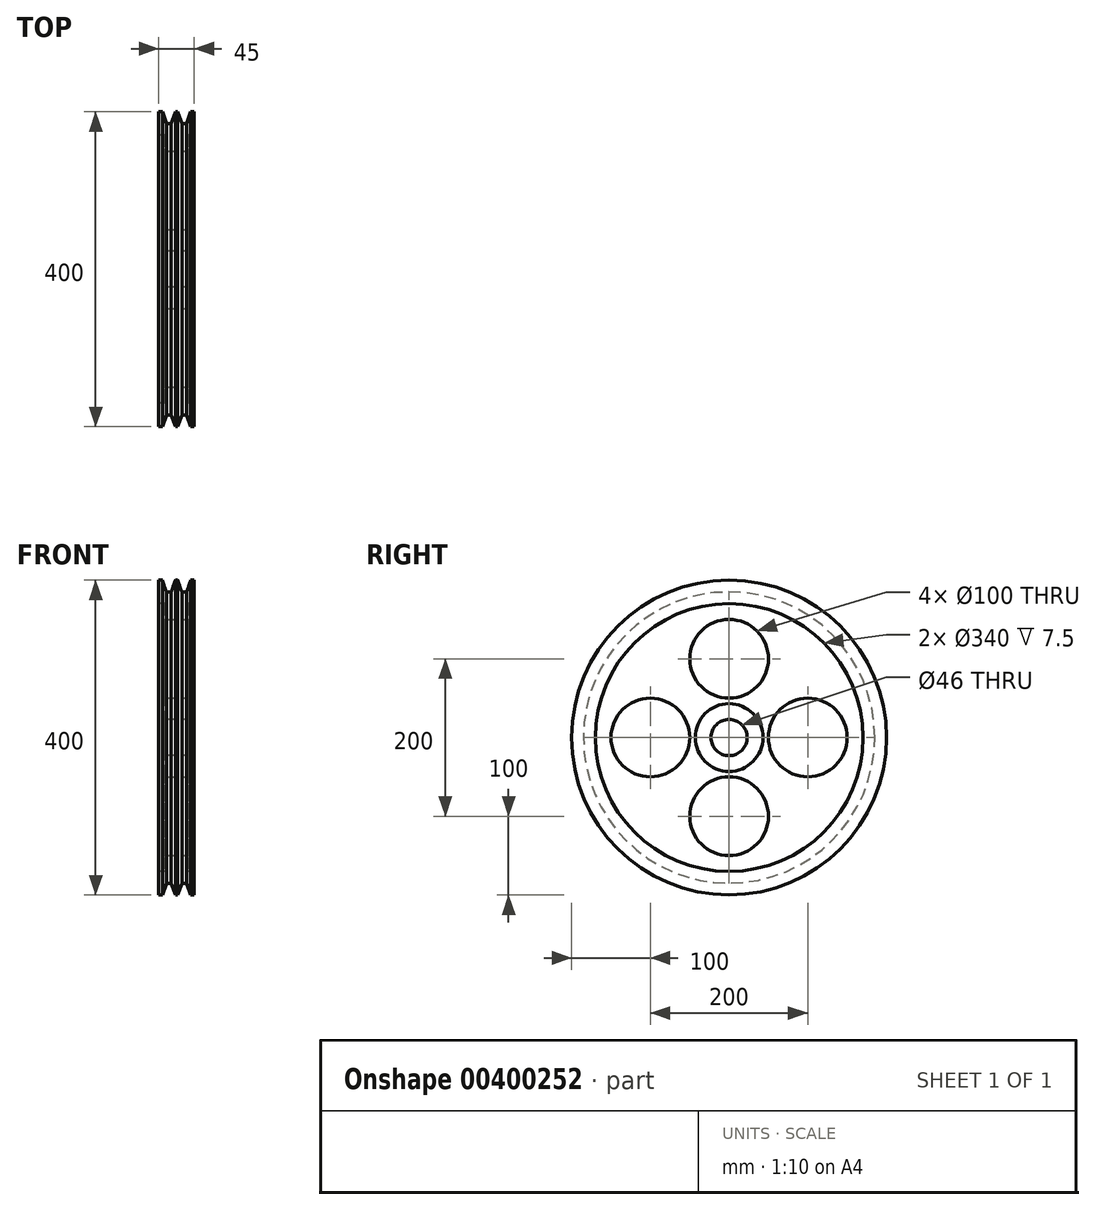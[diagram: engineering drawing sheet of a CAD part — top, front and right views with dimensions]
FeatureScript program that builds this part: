
annotation { "Feature Type Name" : "Feature", "Feature Type Description" : "" }
export const myFeature = defineFeature(function(context is Context, id is Id, definition is map)
    precondition{}
    {
        {
            var Q0;
            Q0=qCreatedBy(makeId("Front.planeOp"),FACE);
            var sketch = newSketch(context, id + "F0", { "sketchPlane" : qUnion([Q0])});
            skLineSegment(sketch, "E0", {"start": v(0, 0) * mm, "end": v(0, 346.48) * mm, "construction": true});
            skLineSegment(sketch, "E1", {"start": v(0, 170) * mm, "end": v(22.5, 170) * mm});
            skLineSegment(sketch, "E2", {"start": v(22.5, 200) * mm, "end": v(22.5, 170) * mm});
            skLineSegment(sketch, "E3", {"start": v(22.5, 200) * mm, "end": v(18, 200) * mm});
            skLineSegment(sketch, "E4", {"start": v(18, 200) * mm, "end": v(12.69, 185) * mm});
            skPoint(sketch, "E5.endSnap0", {"position": v(0, 170) * mm});
            skLineSegment(sketch, "E6", {"start": v(12.69, 185) * mm, "end": v(6.81, 185) * mm});
            skLineSegment(sketch, "E7", {"start": v(1.5, 200) * mm, "end": v(6.81, 185) * mm});
            skLineSegment(sketch, "E8", {"start": v(1.5, 200) * mm, "end": v(0, 200) * mm});
            skLineSegment(sketch, "E9.MirrorCS", {"start": v(-1.5, 200) * mm, "end": v(0, 200) * mm});
            skLineSegment(sketch, "E10.MirrorCS", {"start": v(-18, 200) * mm, "end": v(-12.69, 185) * mm});
            skLineSegment(sketch, "E11.MirrorCS", {"start": v(-12.69, 185) * mm, "end": v(-6.81, 185) * mm});
            skLineSegment(sketch, "E12.MirrorCS", {"start": v(0, 170) * mm, "end": v(-22.5, 170) * mm});
            skLineSegment(sketch, "E13.MirrorCS", {"start": v(-22.5, 200) * mm, "end": v(-18, 200) * mm});
            skLineSegment(sketch, "E14.MirrorCS", {"start": v(-22.5, 200) * mm, "end": v(-22.5, 170) * mm});
            skLineSegment(sketch, "E15.MirrorCS", {"start": v(-1.5, 200) * mm, "end": v(-6.81, 185) * mm});
            skLineSegment(sketch, "E16", {"start": v(9.75, 324.63) * mm, "end": v(9.75, 235.55) * mm, "construction": true});
            skLineSegment(sketch, "E17.bottom", {"start": v(-15, 170) * mm, "end": v(15, 170) * mm});
            skLineSegment(sketch, "E17.top", {"start": v(-109.28, 0) * mm, "end": v(109, 0) * mm, "construction": true});
            skLineSegment(sketch, "E17.left", {"start": v(-15, 170) * mm, "end": v(-15, 23) * mm});
            skLineSegment(sketch, "E17.right", {"start": v(15, 170) * mm, "end": v(15, 43) * mm});
            skLineSegment(sketch, "E18", {"start": v(-15, 23) * mm, "end": v(20, 23) * mm});
            skLineSegment(sketch, "E19", {"start": v(20, 23) * mm, "end": v(20, 43) * mm});
            skLineSegment(sketch, "E20", {"start": v(20, 43) * mm, "end": v(15, 43) * mm});
            skSolve(sketch);
        }
        {
            var Q0;
            Q0 = qSketchRegion(id + "F0", true);
            var Q1;
            Q1=sQuery(id+"F0.wireOp",EDGE,"E17.top");
            revolve(context, id + "F1", {"entities" : qUnion([Q0]), "axis" : qUnion([Q1]), "revolveType" : RevolveType.FULL});
        }
        {
            var Q0;
            Q0=qCreatedBy(makeId("Right.planeOp"),FACE);
            var sketch = newSketch(context, id + "F2", { "sketchPlane" : qUnion([Q0])});
            skLineSegment(sketch, "E21", {"start": v(390.11, 0) * mm, "end": v(-406.35, 0) * mm, "construction": true});
            skLineSegment(sketch, "E22", {"start": v(0, -377) * mm, "end": v(0, 489.97) * mm, "construction": true});
            skCircle(sketch, "E23", {"center": v(0, -100) * mm, "radius": 50 * mm});
            skCircle(sketch, "E24", {"center": v(100, 0) * mm, "radius": 50 * mm});
            skCircle(sketch, "E25.MirrorC", {"center": v(-100, 0) * mm, "radius": 50 * mm});
            skCircle(sketch, "E26.MirrorC", {"center": v(0, 100) * mm, "radius": 50 * mm});
            skSolve(sketch);
        }
        {
            var Q0;
            Q0 = qSketchRegion(id + "F2", true);
            extrude(context, id + "F3", {"entities" : qUnion([Q0]), "operationType" : NewBodyOperationType.REMOVE, "oppositeDirection" : true, "depth" : 50 * mm, "hasSecondDirection" : true, "secondDirectionOppositeDirection" : false, "secondDirectionDepth" : 50 * mm});
        }
    });
